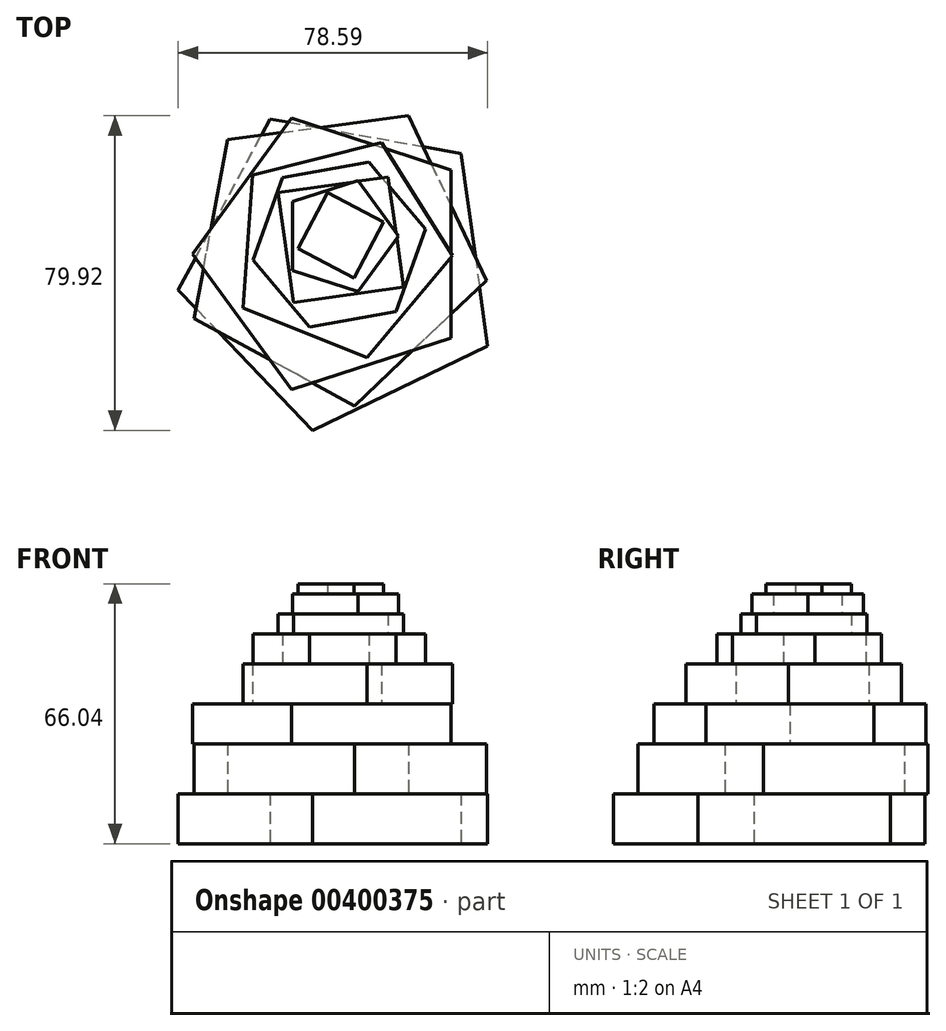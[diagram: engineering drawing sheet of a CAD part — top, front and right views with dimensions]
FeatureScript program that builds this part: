
annotation { "Feature Type Name" : "Feature", "Feature Type Description" : "" }
export const myFeature = defineFeature(function(context is Context, id is Id, definition is map)
    precondition{}
    {
        {
            var Q0;
            Q0=qCreatedBy(makeId("Top.planeOp"),FACE);
            var sketch = newSketch(context, id + "F0", { "sketchPlane" : qUnion([Q0])});
            skCircle(sketch, "E0.cCircle", {"center": v(-37.4, 30.58) * mm, "radius": 33.96 * mm, "construction": true});
            skLineSegment(sketch, "E0.0", {"start": v(-0.4, 10.74) * mm, "end": v(-44.84, -10.74) * mm});
            skLineSegment(sketch, "E0.1", {"start": v(-44.84, -10.74) * mm, "end": v(-78.99, 24.89) * mm});
            skLineSegment(sketch, "E0.2", {"start": v(-78.99, 24.89) * mm, "end": v(-55.66, 68.38) * mm});
            skLineSegment(sketch, "E0.3", {"start": v(-55.66, 68.38) * mm, "end": v(-7.1, 59.63) * mm});
            skLineSegment(sketch, "E0.4", {"start": v(-7.1, 59.63) * mm, "end": v(-0.4, 10.74) * mm});
            skPoint(sketch, "E0.0.midPoint", {"position": v(-22.62, 0) * mm});
            skSolve(sketch);
        }
        {
            var Q0;
            Q0 = qSketchRegion(id + "F0", true);
            extrude(context, id + "F1", {"entities" : qUnion([Q0]), "depth" : 12.7 * mm});
        }
        {
            var Q0;
            Q0=makeQuery(id+"F1.opExtrude","CAP_FACE",FACE,{"disambiguationData":[OSD([sQuery(id+"F0.wireOp",EDGE,"E0.0"),sQuery(id+"F0.wireOp",EDGE,"E0.1"),sQuery(id+"F0.wireOp",EDGE,"E0.2"),sQuery(id+"F0.wireOp",EDGE,"E0.3"),sQuery(id+"F0.wireOp",EDGE,"E0.4")])],"isStart":false});
            var sketch = newSketch(context, id + "F2", { "sketchPlane" : qUnion([Q0])});
            skCircle(sketch, "E1.cCircle", {"center": v(-39.34, 34.56) * mm, "radius": 31.88 * mm, "construction": true});
            skLineSegment(sketch, "E1.0", {"start": v(-74.9, 17.6) * mm, "end": v(-66.45, 63.15) * mm});
            skLineSegment(sketch, "E1.1", {"start": v(-66.45, 63.15) * mm, "end": v(-20.53, 69.18) * mm});
            skLineSegment(sketch, "E1.2", {"start": v(-20.53, 69.18) * mm, "end": v(-0.6, 27.37) * mm});
            skLineSegment(sketch, "E1.3", {"start": v(-0.6, 27.37) * mm, "end": v(-34.2, -4.5) * mm});
            skLineSegment(sketch, "E1.4", {"start": v(-34.2, -4.5) * mm, "end": v(-74.9, 17.6) * mm});
            skPoint(sketch, "E1.0.midPoint", {"position": v(-70.68, 40.38) * mm});
            skSolve(sketch);
        }
        {
            var Q0;
            Q0 = qSketchRegion(id + "F2", true);
            extrude(context, id + "F3", {"entities" : qUnion([Q0]), "depth" : 12.7 * mm});
        }
        {
            var Q0;
            Q0=makeQuery(id+"F3.opExtrude","CAP_FACE",FACE,{"disambiguationData":[OSD([sQuery(id+"F2.wireOp",EDGE,"E1.0"),sQuery(id+"F2.wireOp",EDGE,"E1.1"),sQuery(id+"F2.wireOp",EDGE,"E1.2"),sQuery(id+"F2.wireOp",EDGE,"E1.3"),sQuery(id+"F2.wireOp",EDGE,"E1.4")])],"isStart":false});
            var sketch = newSketch(context, id + "F4", { "sketchPlane" : qUnion([Q0])});
            skCircle(sketch, "E2.cCircle", {"center": v(-39.03, 34.1) * mm, "radius": 29.36 * mm, "construction": true});
            skLineSegment(sketch, "E2.0", {"start": v(-9.67, 55.43) * mm, "end": v(-9.67, 12.76) * mm});
            skLineSegment(sketch, "E2.1", {"start": v(-9.67, 12.76) * mm, "end": v(-50.25, -0.43) * mm});
            skLineSegment(sketch, "E2.2", {"start": v(-50.25, -0.43) * mm, "end": v(-75.33, 34.1) * mm});
            skLineSegment(sketch, "E2.3", {"start": v(-75.33, 34.1) * mm, "end": v(-50.25, 68.61) * mm});
            skLineSegment(sketch, "E2.4", {"start": v(-50.25, 68.61) * mm, "end": v(-9.67, 55.43) * mm});
            skPoint(sketch, "E2.0.midPoint", {"position": v(-9.67, 34.1) * mm});
            skSolve(sketch);
        }
        {
            var Q0;
            Q0 = qSketchRegion(id + "F4", true);
            extrude(context, id + "F5", {"entities" : qUnion([Q0]), "operationType" : NewBodyOperationType.ADD, "depth" : 10.16 * mm});
        }
        {
            var Q0;
            Q0=makeQuery(id+"F5.opExtrude","CAP_FACE",FACE,{"disambiguationData":[OSD([sQuery(id+"F4.wireOp",EDGE,"E2.0"),sQuery(id+"F4.wireOp",EDGE,"E2.1"),sQuery(id+"F4.wireOp",EDGE,"E2.2"),sQuery(id+"F4.wireOp",EDGE,"E2.3"),sQuery(id+"F4.wireOp",EDGE,"E2.4")])],"isStart":false});
            var sketch = newSketch(context, id + "F6", { "sketchPlane" : qUnion([Q0])});
            skCircle(sketch, "E3.cCircle", {"center": v(-38.05, 35.67) * mm, "radius": 23.3 * mm, "construction": true});
            skLineSegment(sketch, "E3.0", {"start": v(-62.45, 20.35) * mm, "end": v(-60.16, 54.14) * mm});
            skLineSegment(sketch, "E3.1", {"start": v(-60.16, 54.14) * mm, "end": v(-27.31, 62.4) * mm});
            skLineSegment(sketch, "E3.2", {"start": v(-27.31, 62.4) * mm, "end": v(-9.3, 33.72) * mm});
            skLineSegment(sketch, "E3.3", {"start": v(-9.3, 33.72) * mm, "end": v(-31.02, 7.73) * mm});
            skLineSegment(sketch, "E3.4", {"start": v(-31.02, 7.73) * mm, "end": v(-62.45, 20.35) * mm});
            skPoint(sketch, "E3.0.midPoint", {"position": v(-61.3, 37.25) * mm});
            skSolve(sketch);
        }
        {
            var Q0;
            Q0 = qSketchRegion(id + "F6", true);
            extrude(context, id + "F7", {"entities" : qUnion([Q0]), "depth" : 10.16 * mm});
        }
        {
            var Q0;
            Q0=makeQuery(id+"F7.opExtrude","CAP_FACE",FACE,{"disambiguationData":[OSD([sQuery(id+"F6.wireOp",EDGE,"E3.0"),sQuery(id+"F6.wireOp",EDGE,"E3.1"),sQuery(id+"F6.wireOp",EDGE,"E3.2"),sQuery(id+"F6.wireOp",EDGE,"E3.3"),sQuery(id+"F6.wireOp",EDGE,"E3.4")])],"isStart":false});
            var sketch = newSketch(context, id + "F8", { "sketchPlane" : qUnion([Q0])});
            skCircle(sketch, "E4.cCircle", {"center": v(-38.05, 36.46) * mm, "radius": 19.26 * mm, "construction": true});
            skLineSegment(sketch, "E4.0", {"start": v(-59.93, 32.5) * mm, "end": v(-52.42, 53.43) * mm});
            skLineSegment(sketch, "E4.1", {"start": v(-52.42, 53.43) * mm, "end": v(-30.54, 57.4) * mm});
            skLineSegment(sketch, "E4.2", {"start": v(-30.54, 57.4) * mm, "end": v(-16.16, 40.42) * mm});
            skLineSegment(sketch, "E4.3", {"start": v(-16.16, 40.42) * mm, "end": v(-23.67, 19.49) * mm});
            skLineSegment(sketch, "E4.4", {"start": v(-23.67, 19.49) * mm, "end": v(-45.56, 15.52) * mm});
            skLineSegment(sketch, "E4.5", {"start": v(-45.56, 15.52) * mm, "end": v(-59.93, 32.5) * mm});
            skPoint(sketch, "E4.0.midPoint", {"position": v(-56.18, 42.96) * mm});
            skSolve(sketch);
        }
        {
            var Q0;
            Q0 = qSketchRegion(id + "F8", true);
            extrude(context, id + "F9", {"entities" : qUnion([Q0]), "depth" : 7.62 * mm});
        }
        {
            var Q0;
            Q0=makeQuery(id+"F9.opExtrude","CAP_FACE",FACE,{"disambiguationData":[OSD([sQuery(id+"F8.wireOp",EDGE,"E4.0"),sQuery(id+"F8.wireOp",EDGE,"E4.1"),sQuery(id+"F8.wireOp",EDGE,"E4.2"),sQuery(id+"F8.wireOp",EDGE,"E4.3"),sQuery(id+"F8.wireOp",EDGE,"E4.4"),sQuery(id+"F8.wireOp",EDGE,"E4.5")])],"isStart":false});
            var sketch = newSketch(context, id + "F10", { "sketchPlane" : qUnion([Q0])});
            skCircle(sketch, "E5.cCircle", {"center": v(-37.65, 37.64) * mm, "radius": 14.13 * mm, "construction": true});
            skLineSegment(sketch, "E5.0", {"start": v(-49.67, 21.68) * mm, "end": v(-53.62, 49.66) * mm});
            skLineSegment(sketch, "E5.1", {"start": v(-53.62, 49.66) * mm, "end": v(-25.63, 53.6) * mm});
            skLineSegment(sketch, "E5.2", {"start": v(-25.63, 53.6) * mm, "end": v(-21.7, 25.62) * mm});
            skLineSegment(sketch, "E5.3", {"start": v(-21.7, 25.62) * mm, "end": v(-49.67, 21.68) * mm});
            skPoint(sketch, "E5.0.midPoint", {"position": v(-51.65, 35.67) * mm});
            skSolve(sketch);
        }
        {
            var Q0;
            Q0 = qSketchRegion(id + "F10", true);
            extrude(context, id + "F11", {"entities" : qUnion([Q0]), "depth" : 5.08 * mm});
        }
        {
            var Q0;
            Q0=makeQuery(id+"F11.opExtrude","CAP_FACE",FACE,{"disambiguationData":[OSD([sQuery(id+"F10.wireOp",EDGE,"E5.0"),sQuery(id+"F10.wireOp",EDGE,"E5.1"),sQuery(id+"F10.wireOp",EDGE,"E5.2"),sQuery(id+"F10.wireOp",EDGE,"E5.3")])],"isStart":false});
            var sketch = newSketch(context, id + "F12", { "sketchPlane" : qUnion([Q0])});
            skCircle(sketch, "E6.cCircle", {"center": v(-37.85, 38.63) * mm, "radius": 12.02 * mm, "construction": true});
            skLineSegment(sketch, "E6.0", {"start": v(-49.87, 29.9) * mm, "end": v(-49.87, 47.36) * mm});
            skLineSegment(sketch, "E6.1", {"start": v(-49.87, 47.36) * mm, "end": v(-33.26, 52.76) * mm});
            skLineSegment(sketch, "E6.2", {"start": v(-33.26, 52.76) * mm, "end": v(-23, 38.63) * mm});
            skLineSegment(sketch, "E6.3", {"start": v(-23, 38.63) * mm, "end": v(-33.26, 24.5) * mm});
            skLineSegment(sketch, "E6.4", {"start": v(-33.26, 24.5) * mm, "end": v(-49.87, 29.9) * mm});
            skPoint(sketch, "E6.0.midPoint", {"position": v(-49.87, 38.63) * mm});
            skSolve(sketch);
        }
        {
            var Q0;
            Q0 = qSketchRegion(id + "F12", true);
            extrude(context, id + "F13", {"entities" : qUnion([Q0]), "depth" : 5.08 * mm});
        }
        {
            var Q0;
            Q0=makeQuery(id+"F13.opExtrude","CAP_FACE",FACE,{"disambiguationData":[OSD([sQuery(id+"F12.wireOp",EDGE,"E6.0"),sQuery(id+"F12.wireOp",EDGE,"E6.1"),sQuery(id+"F12.wireOp",EDGE,"E6.2"),sQuery(id+"F12.wireOp",EDGE,"E6.3"),sQuery(id+"F12.wireOp",EDGE,"E6.4")])],"isStart":false});
            var sketch = newSketch(context, id + "F14", { "sketchPlane" : qUnion([Q0])});
            skCircle(sketch, "E7.cCircle", {"center": v(-37.65, 38.82) * mm, "radius": 8.02 * mm, "construction": true});
            skLineSegment(sketch, "E7.0", {"start": v(-48.5, 35.47) * mm, "end": v(-41, 49.66) * mm});
            skLineSegment(sketch, "E7.1", {"start": v(-41, 49.66) * mm, "end": v(-26.81, 42.17) * mm});
            skLineSegment(sketch, "E7.2", {"start": v(-26.81, 42.17) * mm, "end": v(-34.3, 27.98) * mm});
            skLineSegment(sketch, "E7.3", {"start": v(-34.3, 27.98) * mm, "end": v(-48.5, 35.47) * mm});
            skPoint(sketch, "E7.0.midPoint", {"position": v(-44.75, 42.57) * mm});
            skSolve(sketch);
        }
        {
            var Q0;
            Q0 = qSketchRegion(id + "F14", true);
            extrude(context, id + "F15", {"entities" : qUnion([Q0]), "depth" : 2.54 * mm});
        }
    });
